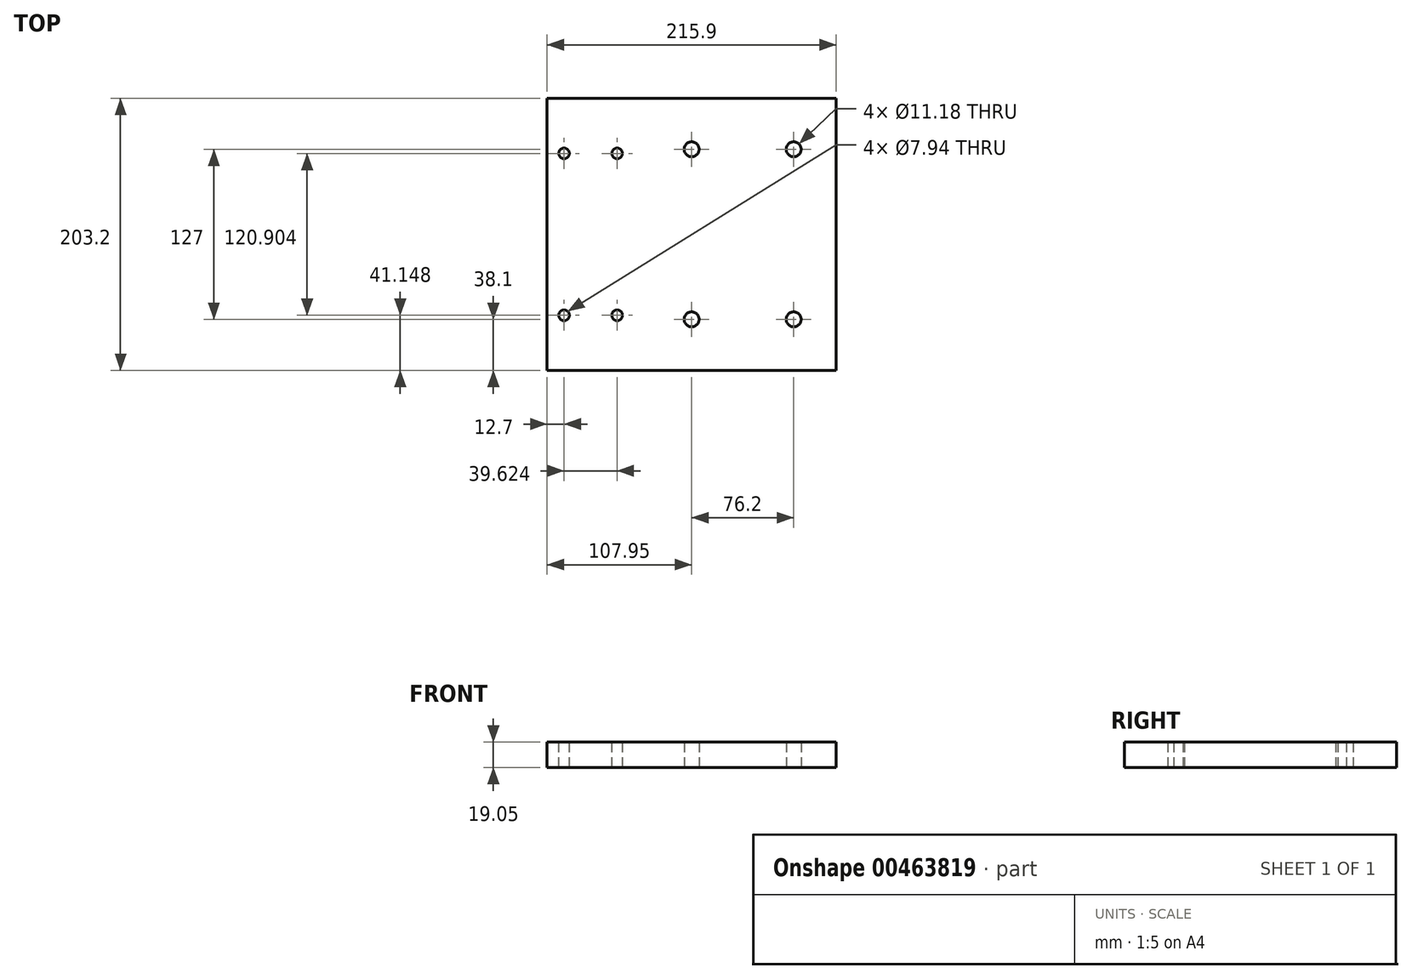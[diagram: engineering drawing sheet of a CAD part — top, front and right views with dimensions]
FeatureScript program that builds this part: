
annotation { "Feature Type Name" : "Feature", "Feature Type Description" : "" }
export const myFeature = defineFeature(function(context is Context, id is Id, definition is map)
    precondition{}
    {
        {
            var Q0;
            Q0=qCreatedBy(makeId("Top.planeOp"),FACE);
            var sketch = newSketch(context, id + "F0", { "sketchPlane" : qUnion([Q0])});
            skLineSegment(sketch, "E0.bottom", {"start": v(-107.95, 101.6) * mm, "end": v(107.95, 101.6) * mm});
            skLineSegment(sketch, "E0.top", {"start": v(-107.95, -101.6) * mm, "end": v(107.95, -101.6) * mm});
            skLineSegment(sketch, "E0.left", {"start": v(-107.95, 101.6) * mm, "end": v(-107.95, -101.6) * mm});
            skLineSegment(sketch, "E0.right", {"start": v(107.95, 101.6) * mm, "end": v(107.95, -101.6) * mm});
            skPoint(sketch, "E0.middle", {"position": v(0, 0) * mm});
            skLineSegment(sketch, "E1.0", {"start": v(38.1, 101.6) * mm, "end": v(38.1, -101.6) * mm, "construction": true});
            skLineSegment(sketch, "E2.0", {"start": v(0, 101.6) * mm, "end": v(0, -101.6) * mm, "construction": true});
            skLineSegment(sketch, "E3", {"start": v(-136.26, 0) * mm, "end": v(140.71, 0) * mm, "construction": true});
            skLineSegment(sketch, "E4.0", {"start": v(-136.26, -63.5) * mm, "end": v(140.71, -63.5) * mm, "construction": true});
            skPoint(sketch, "E5", {"position": v(0, -63.5) * mm});
            skPoint(sketch, "E6.MirrorP", {"position": v(0, 63.5) * mm});
            skPoint(sketch, "E7.MirrorP", {"position": v(76.2, 63.5) * mm});
            skPoint(sketch, "E8.MirrorP", {"position": v(76.2, -63.5) * mm});
            skSolve(sketch);
        }
        {
            var Q0;
            Q0=qSketchRegion(id+"F0",true);
            extrude(context, id + "F1", {"entities" : qUnion([Q0]), "depth" : 19.05 * mm});
        }
        {
            var Q0;
            Q0=sQuery(id+"F0.wireOp",VERTEX,"E6.MirrorP");
            var Q1;
            Q1=sQuery(id+"F0.wireOp",VERTEX,"E7.MirrorP");
            var Q2;
            Q2=sQuery(id+"F0.wireOp",VERTEX,"E5");
            var Q3;
            Q3=sQuery(id+"F0.wireOp",VERTEX,"E8.MirrorP");
            var Q4;
            Q4=makeQuery(id+"F1.opExtrude","SWEPT_BODY",BODY,{"disambiguationData":[OSD([sQuery(id+"F0.wireOp",EDGE,"E0.bottom"),sQuery(id+"F0.wireOp",EDGE,"E0.top"),sQuery(id+"F0.wireOp",EDGE,"E0.left"),sQuery(id+"F0.wireOp",EDGE,"E0.right")])]});
            hole(context, id + "F2", {"style" : HoleStyle.SIMPLE, "endStyle" : HoleEndStyle.THROUGH, "oppositeDirection" : true, "holeDiameter" : 11.18 * mm, "isTappedThrough" : true, "tappedDepth" : 12.06 * mm, "tapClearance" : 3, "startFromSketch" : true, "locations" : qUnion([Q0, Q1, Q2, Q3]), "scope" : qUnion([Q4])});
        }
        {
            var Q0;
            Q0=makeQuery(id+"F1.opExtrude","CAP_FACE",FACE,{"disambiguationData":[OSD([sQuery(id+"F0.wireOp",EDGE,"E0.bottom"),sQuery(id+"F0.wireOp",EDGE,"E0.top"),sQuery(id+"F0.wireOp",EDGE,"E0.left"),sQuery(id+"F0.wireOp",EDGE,"E0.right")])],"isStart":false});
            var sketch = newSketch(context, id + "F3", { "sketchPlane" : qUnion([Q0])});
            skLineSegment(sketch, "E9.0", {"start": v(-95.25, 101.6) * mm, "end": v(-95.25, -101.6) * mm, "construction": true});
            skLineSegment(sketch, "E10.0", {"start": v(-55.63, 101.6) * mm, "end": v(-55.63, -101.6) * mm, "construction": true});
            skLineSegment(sketch, "E11.0", {"start": v(-136.26, 0) * mm, "end": v(140.71, 0) * mm, "construction": true});
            skLineSegment(sketch, "E12.0", {"start": v(-136.26, -60.45) * mm, "end": v(140.71, -60.45) * mm, "construction": true});
            skPoint(sketch, "E13", {"position": v(-95.25, -60.45) * mm});
            skPoint(sketch, "E14", {"position": v(-55.63, -60.45) * mm});
            skPoint(sketch, "E15.MirrorP", {"position": v(-95.25, 60.45) * mm});
            skPoint(sketch, "E16.MirrorP", {"position": v(-55.63, 60.45) * mm});
            skSolve(sketch);
        }
        {
            var Q0;
            Q0=sQuery(id+"F3.wireOp",VERTEX,"E15.MirrorP");
            var Q1;
            Q1=sQuery(id+"F3.wireOp",VERTEX,"E16.MirrorP");
            var Q2;
            Q2=sQuery(id+"F3.wireOp",VERTEX,"E13");
            var Q3;
            Q3=sQuery(id+"F3.wireOp",VERTEX,"E14");
            var Q4;
            Q4=makeQuery(id+"F1.opExtrude","SWEPT_BODY",BODY,{"disambiguationData":[OSD([sQuery(id+"F0.wireOp",EDGE,"E0.bottom"),sQuery(id+"F0.wireOp",EDGE,"E0.top"),sQuery(id+"F0.wireOp",EDGE,"E0.left"),sQuery(id+"F0.wireOp",EDGE,"E0.right")])]});
            hole(context, id + "F4", {"style" : HoleStyle.SIMPLE, "endStyle" : HoleEndStyle.THROUGH, "standardTappedOrClearance" : lookupTablePath({ "standard" : "ANSI", "engagement" : "75%", "pitch" : "16 tpi", "size" : "3/8", "type" : "Tapped" }), "standardBlindInLast" : lookupTablePath({ "standard" : "ANSI", "engagement" : "75%", "pitch" : "16 tpi", "size" : "3/8", "type" : "Tapped" }), "holeDiameter" : 7.94 * mm, "showTappedDepth" : true, "isTappedThrough" : true, "tappedDepth" : 12.06 * mm, "tapClearance" : 3, "startFromSketch" : true, "locations" : qUnion([Q0, Q1, Q2, Q3]), "scope" : qUnion([Q4]), "majorDiameter" : 9.53 * mm});
        }
    });
